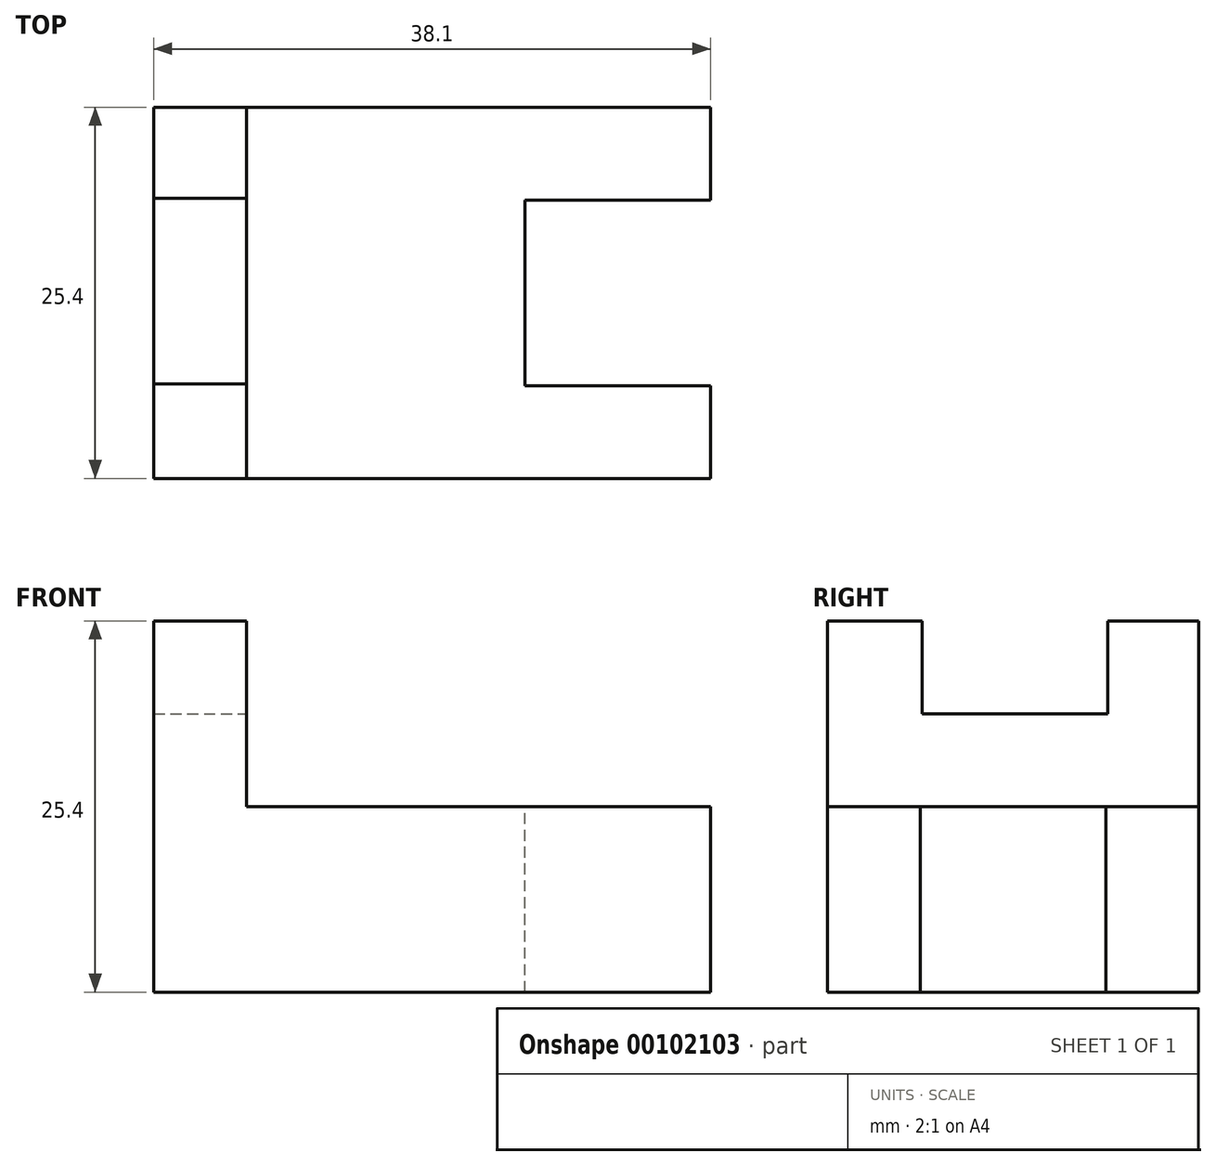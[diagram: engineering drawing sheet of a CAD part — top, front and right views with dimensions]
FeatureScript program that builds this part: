
annotation { "Feature Type Name" : "Feature", "Feature Type Description" : "" }
export const myFeature = defineFeature(function(context is Context, id is Id, definition is map)
    precondition{}
    {
        {
            var Q0;
            Q0=qCreatedBy(makeId("Front.planeOp"),FACE);
            var sketch = newSketch(context, id + "F0", { "sketchPlane" : qUnion([Q0])});
            skLineSegment(sketch, "E0", {"start": v(0, 0) * mm, "end": v(-38.1, 0) * mm});
            skLineSegment(sketch, "E1", {"start": v(-38.1, 0) * mm, "end": v(-38.1, 25.4) * mm});
            skLineSegment(sketch, "E2", {"start": v(-38.1, 25.4) * mm, "end": v(-31.75, 25.4) * mm});
            skLineSegment(sketch, "E3", {"start": v(-31.75, 25.4) * mm, "end": v(-31.75, 12.7) * mm});
            skLineSegment(sketch, "E4", {"start": v(-31.75, 12.7) * mm, "end": v(0, 12.7) * mm});
            skLineSegment(sketch, "E5", {"start": v(0, 12.7) * mm, "end": v(0, 0) * mm});
            skSolve(sketch);
        }
        {
            var Q0;
            Q0 = qSketchRegion(id + "F0", true);
            extrude(context, id + "F1", {"entities" : qUnion([Q0]), "endBound" : BoundingType.SYMMETRIC, "depth" : 25.4 * mm});
        }
        {
            var Q0;
            Q0=qCreatedBy(makeId("Right.planeOp"),FACE);
            var sketch = newSketch(context, id + "F2", { "sketchPlane" : qUnion([Q0])});
            skLineSegment(sketch, "E6.bottom", {"start": v(-6.23, 25.4) * mm, "end": v(6.47, 25.4) * mm});
            skLineSegment(sketch, "E6.top", {"start": v(-6.23, 19.05) * mm, "end": v(6.47, 19.05) * mm});
            skLineSegment(sketch, "E6.left", {"start": v(-6.23, 25.4) * mm, "end": v(-6.23, 19.05) * mm});
            skLineSegment(sketch, "E6.right", {"start": v(6.47, 25.4) * mm, "end": v(6.47, 19.05) * mm});
            skSolve(sketch);
        }
        {
            var Q0;
            Q0 = qSketchRegion(id + "F2", true);
            extrude(context, id + "F3", {"entities" : qUnion([Q0]), "operationType" : NewBodyOperationType.REMOVE, "endBound" : BoundingType.THROUGH_ALL, "oppositeDirection" : true, "depth" : 25.4 * mm});
        }
        {
            var Q0;
            Q0=qCreatedBy(makeId("Right.planeOp"),FACE);
            var sketch = newSketch(context, id + "F4", { "sketchPlane" : qUnion([Q0])});
            skLineSegment(sketch, "E7.bottom", {"start": v(-6.35, 0) * mm, "end": v(6.35, 0) * mm});
            skLineSegment(sketch, "E7.top", {"start": v(-6.35, 12.7) * mm, "end": v(6.35, 12.7) * mm});
            skLineSegment(sketch, "E7.left", {"start": v(-6.35, 0) * mm, "end": v(-6.35, 12.7) * mm});
            skLineSegment(sketch, "E7.right", {"start": v(6.35, 0) * mm, "end": v(6.35, 12.7) * mm});
            skSolve(sketch);
        }
        {
            var Q0;
            Q0 = qSketchRegion(id + "F4", true);
            extrude(context, id + "F5", {"entities" : qUnion([Q0]), "operationType" : NewBodyOperationType.REMOVE, "oppositeDirection" : true, "depth" : 12.7 * mm});
        }
    });
